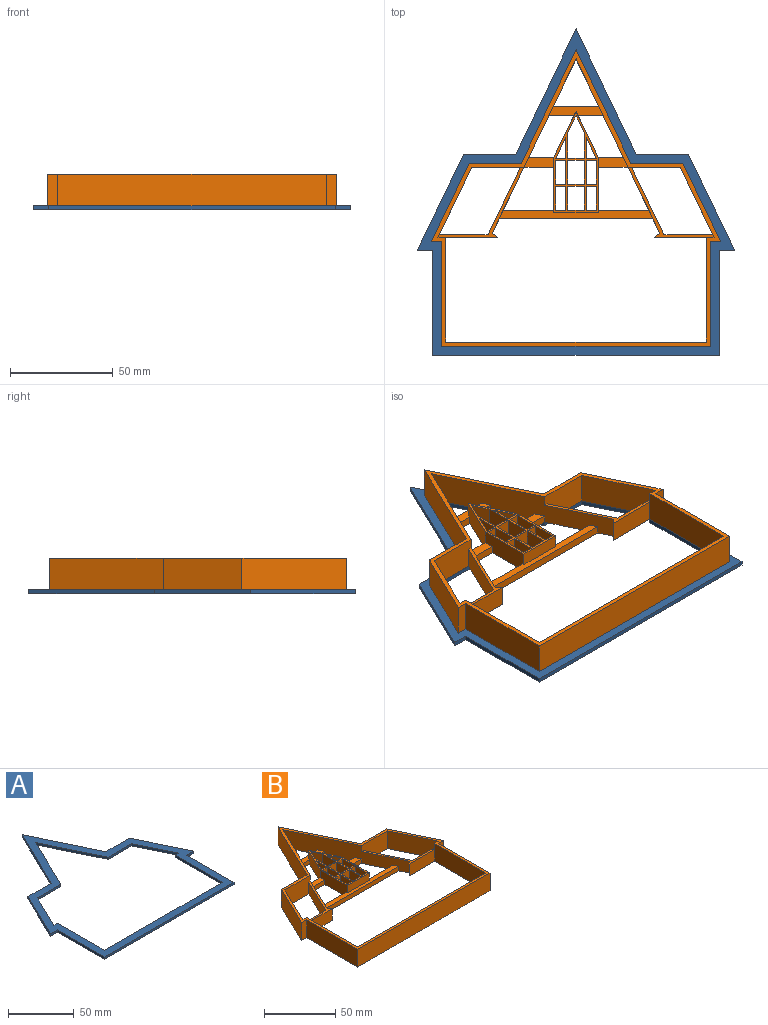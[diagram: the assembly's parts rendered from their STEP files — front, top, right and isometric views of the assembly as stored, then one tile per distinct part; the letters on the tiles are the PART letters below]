
ASSEMBLY  parts=2 mates=1
PART A: 24 faces, bbox 154.8x159x2 mm
  f0: plane 50.8x2.03mm, normal (-1,0,0), area 103.2mm2, adj f1,f21,f22,f23
  f1: plane 139.7x2.03mm, normal (0,-1,0), area 283.9mm2, adj f0,f2,f22,f23
  f2: plane 50.8x2.03mm, normal (1,0,0), area 103.2mm2, adj f1,f3,f22,f23
  f3: plane 7.56x2.03mm, normal (0,-1,0), area 15.4mm2, adj f2,f4,f22,f23
  f4: plane 47.04x22.62mm, normal (0.9,0.43,0), area 106.1mm2, adj f3,f5,f22,f23
  f5: plane 25.4x2.03mm, normal (0,1,0), area 51.6mm2, adj f4,f6,f22,f23
  f6: plane 61.13x29.39mm, normal (0.9,0.43,0), area 137.8mm2, adj f5,f7,f22,f23
  f7: plane 61.13x29.39mm, normal (-0.9,0.43,0), area 137.8mm2, adj f6,f8,f22,f23
  f8: plane 25.4x2.03mm, normal (0,1,0), area 51.6mm2, adj f7,f9,f22,f23
  f9: plane 47.04x22.62mm, normal (-0.9,0.43,0), area 106.1mm2, adj f8,f21,f22,f23
  f10: plane 3.81x2.03mm, normal (0,1,0), area 7.7mm2, adj f11,f20,f22,f23
  f11: plane 50.8x2.03mm, normal (-1,0,0), area 103.2mm2, adj f10,f12,f22,f23
  f12: plane 127x2.03mm, normal (0,1,0), area 258.1mm2, adj f11,f13,f22,f23
  f13: plane 50.8x2.03mm, normal (1,0,0), area 103.2mm2, adj f12,f14,f22,f23
  f14: plane 3.81x2.03mm, normal (0,1,0), area 7.7mm2, adj f13,f15,f22,f23
  f15: plane 34.34x16.51mm, normal (0.9,-0.43,0), area 77.4mm2, adj f14,f16,f22,f23
  f16: plane 25.4x2.03mm, normal (0,-1,0), area 51.6mm2, adj f15,f17,f22,f23
  f17: plane 52.83x25.4mm, normal (0.9,-0.43,0), area 119.1mm2, adj f16,f18,f22,f23
  f18: plane 52.83x25.4mm, normal (-0.9,-0.43,0), area 119.1mm2, adj f17,f19,f22,f23
  f19: plane 25.4x2.03mm, normal (0,-1,0), area 51.6mm2, adj f18,f20,f22,f23
  f20: plane 34.34x16.51mm, normal (-0.9,-0.43,0), area 77.4mm2, adj f10,f19,f22,f23
  f21: plane 7.56x2.03mm, normal (0,-1,0), area 15.4mm2, adj f0,f9,f22,f23
  f22: plane 158.97x154.82mm, normal (0,0,-1), area 3263mm2, adj f0,f1,f2,f3,f4,f5,f6,f7
  f23: plane 158.97x154.82mm, normal (0,0,1), area 3263mm2, adj f0,f1,f2,f3,f4,f5,f6,f7
PART B: 89 faces, bbox 141.1x144.7x15.2 mm
  f0: plane 25.4x15.24mm, normal (0,-1,0), area 369.9mm2, adj f6,f7,f22,f23,f31,f33
  f1: plane 5.08x3.81mm, normal (0,1,0), area 19.4mm2, adj f2,f21,f22,f28
  f2: plane 50.8x15.24mm, normal (-1,0,0), area 774.2mm2, adj f1,f3,f22,f23,f24
  f3: plane 127x15.24mm, normal (0,1,0), area 1935.5mm2, adj f2,f4,f22,f23
  f4: plane 50.8x15.24mm, normal (1,0,0), area 774.2mm2, adj f3,f5,f22,f23,f29
  f5: plane 5.08x3.81mm, normal (0,1,0), area 19.4mm2, adj f4,f6,f22,f33
  f6: plane 34.34x16.51mm, normal (0.9,-0.43,0), area 563.5mm2, adj f0,f5,f22,f23,f32,f33
  f7: plane 84.87x40.81mm, normal (0.9,-0.43,0), area 1199.3mm2, adj f0,f8,f22,f23,f30,f33,f75,f77
  f8: plane 84.87x40.81mm, normal (-0.9,-0.43,0), area 1199.3mm2, adj f7,f9,f22,f23,f27,f28,f75,f76
  f9: plane 25.4x15.24mm, normal (0,-1,0), area 369.9mm2, adj f8,f21,f22,f23,f26,f28
  f10: plane 50.8x15.24mm, normal (-1,0,0), area 774.2mm2, adj f11,f20,f22,f23
  f11: plane 131.06x15.24mm, normal (0,-1,0), area 1997.4mm2, adj f10,f12,f22,f23
  f12: plane 50.8x15.24mm, normal (1,0,0), area 774.2mm2, adj f11,f13,f22,f23
  f13: plane 15.24x5.01mm, normal (0,-1,0), area 76.3mm2, adj f12,f14,f22,f23
  f14: plane 38.4x18.46mm, normal (0.9,0.43,0), area 649.4mm2, adj f13,f15,f22,f23
  f15: plane 25.4x15.24mm, normal (0,1,0), area 387.1mm2, adj f14,f16,f22,f23
  f16: plane 55.48x26.68mm, normal (0.9,0.43,0), area 938.2mm2, adj f15,f17,f22,f23
  f17: plane 55.48x26.68mm, normal (-0.9,0.43,0), area 938.2mm2, adj f16,f18,f22,f23
  f18: plane 25.4x15.24mm, normal (0,1,0), area 387.1mm2, adj f17,f19,f22,f23
  f19: plane 38.4x18.46mm, normal (-0.9,0.43,0), area 649.4mm2, adj f18,f20,f22,f23
  f20: plane 15.24x5.01mm, normal (0,-1,0), area 76.3mm2, adj f10,f19,f22,f23
  f21: plane 34.34x16.51mm, normal (-0.9,-0.43,0), area 563.5mm2, adj f1,f9,f22,f23,f25,f28
  f22: plane 144.68x141.08mm, normal (0,0,1), area 998mm2, adj f0,f1,f2,f3,f4,f5,f6,f7
  f23: plane 144.68x141.08mm, normal (0,0,-1), area 1918.8mm2, adj f0,f2,f3,f4,f6,f7,f8,f9
  f24: plane 25.4x10.16mm, normal (0,-1,0), area 258.1mm2, adj f2,f23,f27,f28
  f25: plane 23.71x10.16mm, normal (0,1,0), area 240.9mm2, adj f21,f23,f26,f28
  f26: plane 32.81x15.78mm, normal (0.9,0.43,0), area 369.9mm2, adj f9,f23,f25,f28
  f27: plane 10.16x2.71mm, normal (-0.65,0.76,0), area 36mm2, adj f8,f23,f24,f28
  f28: plane 41.91x34.34mm, normal (0,0,1), area 98.6mm2, adj f1,f8,f9,f21,f24,f25,f26,f27
  f29: plane 25.4x10.16mm, normal (0,-1,0), area 258.1mm2, adj f4,f23,f30,f33
  f30: plane 10.16x2.71mm, normal (0.65,0.76,0), area 36mm2, adj f7,f23,f29,f33
  f31: plane 32.81x15.78mm, normal (-0.9,0.43,0), area 369.9mm2, adj f0,f23,f32,f33
  f32: plane 23.71x10.16mm, normal (0,1,0), area 240.9mm2, adj f6,f23,f31,f33
  f33: plane 41.91x34.34mm, normal (0,0,1), area 98.6mm2, adj f0,f5,f6,f7,f29,f30,f31,f32
  f34: plane 26.65x10.16mm, normal (-1,0,0), area 248.9mm2, adj f23,f59,f60,f74,f77,f78,f87,f88
  f35: plane 11.69x10.16mm, normal (-1,0,0), area 118.8mm2, adj f23,f36,f73,f74
  f36: plane 10.16x7.86mm, normal (0,1,0), area 79.9mm2, adj f23,f35,f37,f74
  f37: plane 11.69x10.16mm, normal (1,0,0), area 118.8mm2, adj f23,f36,f73,f74
  f38: plane 10.16x4.95mm, normal (0,1,0), area 50.3mm2, adj f23,f39,f64,f74
  f39: plane 10.3x10.16mm, normal (1,0,0), area 104.7mm2, adj f23,f38,f64,f74
  f40: plane 10.3x10.16mm, normal (-1,0,0), area 104.7mm2, adj f23,f41,f65,f74
  f41: plane 10.16x4.95mm, normal (0,1,0), area 50.3mm2, adj f23,f40,f65,f74
  f42: plane 10.16x4.95mm, normal (0,-1,0), area 50.3mm2, adj f23,f43,f66,f74
  f43: plane 11.69x10.16mm, normal (-1,0,0), area 118.8mm2, adj f23,f42,f44,f74
  f44: plane 10.16x4.95mm, normal (0,1,0), area 50.3mm2, adj f23,f43,f66,f74
  f45: plane 10.16x4.95mm, normal (0,1,0), area 50.3mm2, adj f23,f46,f67,f74
  f46: plane 11.69x10.16mm, normal (1,0,0), area 118.8mm2, adj f23,f45,f47,f74
  f47: plane 10.16x4.95mm, normal (0,-1,0), area 50.3mm2, adj f23,f46,f67,f74
  f48: plane 10.16x7.86mm, normal (0,1,0), area 79.9mm2, adj f23,f49,f68,f74
  f49: plane 11.69x10.16mm, normal (1,0,0), area 118.8mm2, adj f23,f48,f50,f74
  f50: plane 10.16x7.86mm, normal (0,-1,0), area 79.9mm2, adj f23,f49,f68,f74
  f51: plane 11.69x10.16mm, normal (-1,0,0), area 118.8mm2, adj f23,f52,f69,f74
  f52: plane 10.16x4.95mm, normal (0,1,0), area 50.3mm2, adj f23,f51,f53,f74
  f53: plane 11.69x10.16mm, normal (1,0,0), area 118.8mm2, adj f23,f52,f69,f74
  f54: plane 10.16x8.17mm, normal (0.9,-0.43,0), area 92.1mm2, adj f23,f55,f70,f74
  f55: plane 10.16x8.18mm, normal (-0.9,-0.43,0), area 92.2mm2, adj f23,f54,f56,f74
  f56: plane 12.42x10.16mm, normal (-1,0,0), area 126.2mm2, adj f23,f55,f57,f74
  f57: plane 10.16x7.86mm, normal (0,1,0), area 79.9mm2, adj f23,f56,f70,f74
  f58: plane 22.72x10.92mm, normal (0.9,0.43,0), area 246.2mm2, adj f23,f59,f71,f74,f80,f84,f85
  f59: plane 22.72x10.92mm, normal (-0.9,0.43,0), area 246.2mm2, adj f23,f34,f58,f74,f83,f85,f86
  f60: plane 21.84x6.35mm, normal (0,-1,0), area 138.7mm2, adj f34,f71,f74,f78
  f61: plane 11.69x10.16mm, normal (-1,0,0), area 118.8mm2, adj f23,f62,f72,f74
  f62: plane 10.16x4.95mm, normal (0,1,0), area 50.3mm2, adj f23,f61,f63,f74
  f63: plane 11.69x10.16mm, normal (1,0,0), area 118.8mm2, adj f23,f62,f72,f74
  f64: plane 10.3x10.16mm, normal (-0.9,-0.43,0), area 116.1mm2, adj f23,f38,f39,f74
  f65: plane 10.3x10.16mm, normal (0.9,-0.43,0), area 116.1mm2, adj f23,f40,f41,f74
  f66: plane 11.69x10.16mm, normal (1,0,0), area 118.8mm2, adj f23,f42,f44,f74
  f67: plane 11.69x10.16mm, normal (-1,0,0), area 118.8mm2, adj f23,f45,f47,f74
  f68: plane 11.69x10.16mm, normal (-1,0,0), area 118.8mm2, adj f23,f48,f50,f74
  f69: plane 10.16x4.95mm, normal (0,-1,0), area 50.3mm2, adj f23,f51,f53,f74
  f70: plane 12.43x10.16mm, normal (1,0,0), area 126.3mm2, adj f23,f54,f57,f74
  f71: plane 26.65x10.16mm, normal (1,0,0), area 248.9mm2, adj f23,f58,f60,f74,f76,f78,f79,f81
  f72: plane 10.16x4.95mm, normal (0,-1,0), area 50.3mm2, adj f23,f61,f63,f74
  f73: plane 10.16x7.86mm, normal (0,-1,0), area 79.9mm2, adj f23,f35,f37,f74
  f74: plane 49.36x21.84mm, normal (0,0,1), area 233.9mm2, adj f34,f35,f36,f37,f38,f39,f40,f41
  f75: plane 74.58x3.81mm, normal (0,-1,0), area 284.2mm2, adj f7,f8,f23,f78
  f76: plane 24.54x3.81mm, normal (0,1,0), area 93.5mm2, adj f8,f23,f71,f78
  f77: plane 24.54x3.81mm, normal (0,1,0), area 93.5mm2, adj f7,f23,f34,f78
  f78: plane 74.58x3.81mm, normal (0,0,1), area 255.1mm2, adj f7,f8,f34,f60,f71,f75,f76,f77
  f79: plane 14.48x3.81mm, normal (0,-1,0), area 55.2mm2, adj f8,f23,f71,f81
  f80: plane 12.21x3.81mm, normal (0,1,0), area 46.5mm2, adj f8,f23,f58,f81
  f81: plane 14.48x4.71mm, normal (0,0,1), area 62.9mm2, adj f8,f71,f79,f80
  f82: plane 22.3x3.81mm, normal (0,1,0), area 85mm2, adj f7,f8,f23,f85
  f83: plane 12.21x3.81mm, normal (0,-1,0), area 46.5mm2, adj f7,f23,f59,f85
  f84: plane 12.21x3.81mm, normal (0,-1,0), area 46.5mm2, adj f8,f23,f58,f85
  f85: plane 26.68x4.56mm, normal (0,0,1), area 109mm2, adj f7,f8,f58,f59,f82,f83,f84
  f86: plane 12.21x3.81mm, normal (0,1,0), area 46.5mm2, adj f7,f23,f59,f88
  f87: plane 14.48x3.81mm, normal (0,-1,0), area 55.2mm2, adj f7,f23,f34,f88
  f88: plane 14.48x4.71mm, normal (0,0,1), area 62.9mm2, adj f7,f34,f86,f87
PLACE A t=(136.54,55.24,38.04)mm
PLACE B t=(136.54,55.24,38.04)mm
MATE fastened A.f23 <-> B.f23  axis (0,0,1) through (141.3,142.4,38.04)mm
